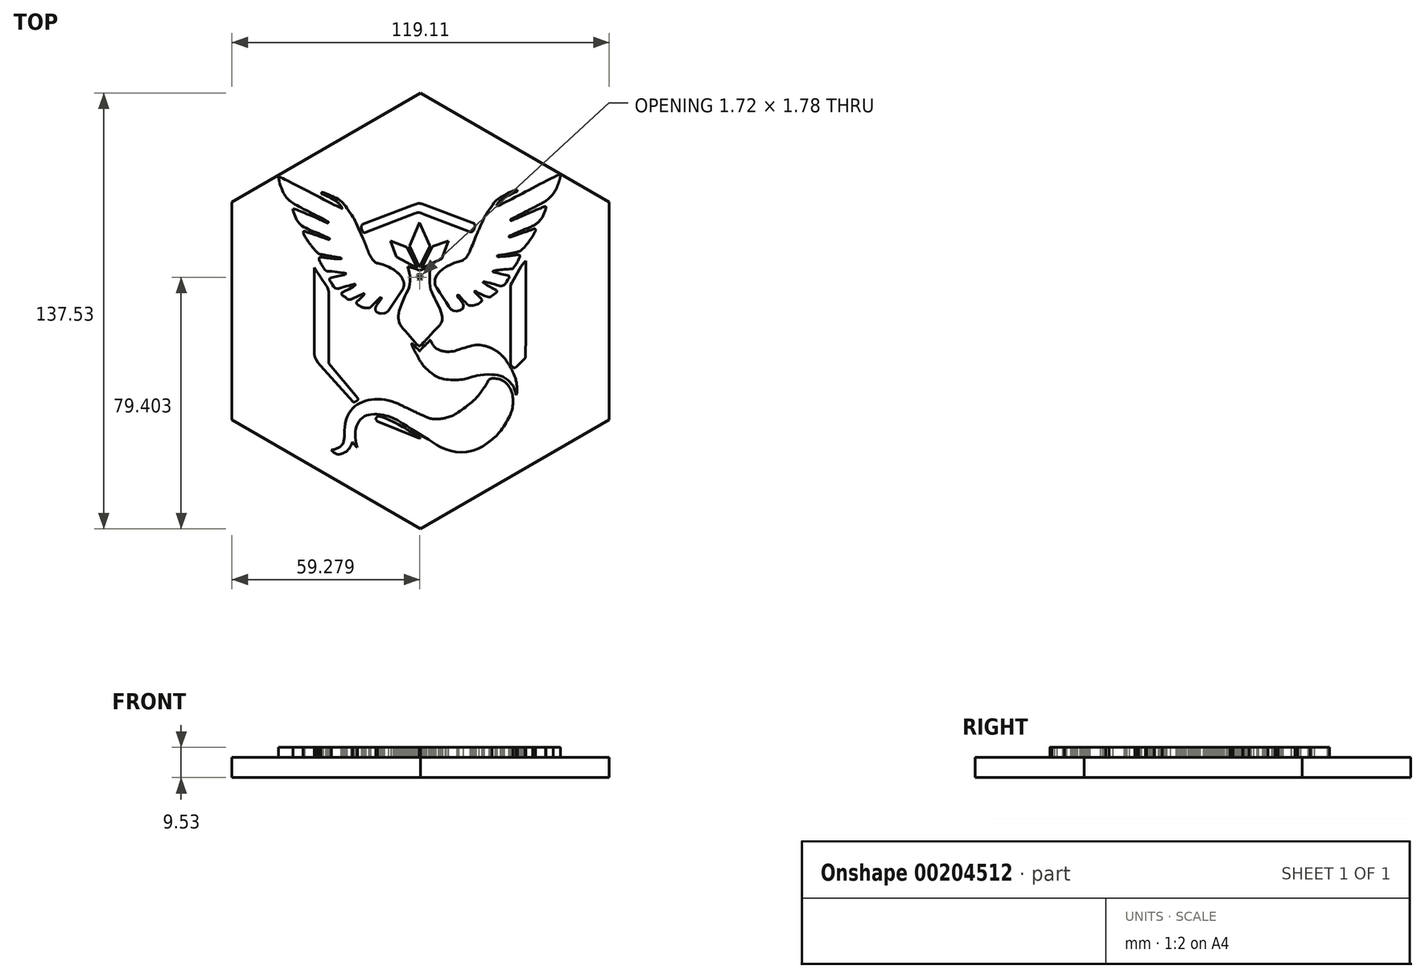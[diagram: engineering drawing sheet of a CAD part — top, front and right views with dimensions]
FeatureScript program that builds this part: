
annotation { "Feature Type Name" : "Feature", "Feature Type Description" : "" }
export const myFeature = defineFeature(function(context is Context, id is Id, definition is map)
    precondition{}
    {
        {
            var Q0;
            Q0=qCreatedBy(makeId("Top.planeOp"),FACE);
            var sketch = newSketch(context, id + "F0", { "sketchPlane" : qUnion([Q0])});
            skCircle(sketch, "E0.cCircle", {"center": v(-105.63, 45.8) * mm, "radius": 59.55 * mm, "construction": true});
            skLineSegment(sketch, "E0.0", {"start": v(-46.08, 80.2) * mm, "end": v(-46.08, 11.43) * mm});
            skLineSegment(sketch, "E0.1", {"start": v(-46.08, 11.43) * mm, "end": v(-105.63, -22.96) * mm});
            skLineSegment(sketch, "E0.2", {"start": v(-105.63, -22.96) * mm, "end": v(-165.19, 11.43) * mm});
            skLineSegment(sketch, "E0.3", {"start": v(-165.19, 11.43) * mm, "end": v(-165.19, 80.2) * mm});
            skLineSegment(sketch, "E0.4", {"start": v(-165.19, 80.2) * mm, "end": v(-105.63, 114.57) * mm});
            skLineSegment(sketch, "E0.5", {"start": v(-105.63, 114.57) * mm, "end": v(-46.08, 80.2) * mm});
            skPoint(sketch, "E0.0.midPoint", {"position": v(-46.08, 45.8) * mm});
            skSolve(sketch);
        }
        {
            var Q0;
            Q0 = qSketchRegion(id + "F0", true);
            extrude(context, id + "F1", {"entities" : qUnion([Q0]), "depth" : 6.35 * mm});
        }
        {
            var Q0;
            Q0=makeQuery(id+"F1.opExtrude","CAP_FACE",FACE,{"disambiguationData":[OSD([sQuery(id+"F0.wireOp",EDGE,"E0.0"),sQuery(id+"F0.wireOp",EDGE,"E0.1"),sQuery(id+"F0.wireOp",EDGE,"E0.2"),sQuery(id+"F0.wireOp",EDGE,"E0.3"),sQuery(id+"F0.wireOp",EDGE,"E0.4"),sQuery(id+"F0.wireOp",EDGE,"E0.5")])],"isStart":false});
            var sketch = newSketch(context, id + "F2", { "sketchPlane" : qUnion([Q0])});
            skLineSegment(sketch, "E1", {"start": v(-105.95, 58.52) * mm, "end": v(-106.29, 58.67) * mm});
            skLineSegment(sketch, "E2", {"start": v(-106.29, 58.67) * mm, "end": v(-106.82, 58.9) * mm});
            skLineSegment(sketch, "E3", {"start": v(-106.82, 58.9) * mm, "end": v(-107.22, 59.06) * mm});
            skLineSegment(sketch, "E4", {"start": v(-107.22, 59.06) * mm, "end": v(-107.95, 59.33) * mm});
            skLineSegment(sketch, "E5", {"start": v(-107.95, 59.33) * mm, "end": v(-108.51, 59.51) * mm});
            skLineSegment(sketch, "E6", {"start": v(-108.51, 59.51) * mm, "end": v(-109.32, 59.76) * mm});
            skLineSegment(sketch, "E7", {"start": v(-109.32, 59.76) * mm, "end": v(-109.7, 59.85) * mm});
            skLineSegment(sketch, "E8", {"start": v(-109.7, 59.85) * mm, "end": v(-109.79, 59.79) * mm});
            skLineSegment(sketch, "E9", {"start": v(-109.79, 59.79) * mm, "end": v(-109.65, 59.44) * mm});
            skLineSegment(sketch, "E10", {"start": v(-109.65, 59.44) * mm, "end": v(-109.46, 58.9) * mm});
            skLineSegment(sketch, "E11", {"start": v(-109.46, 58.9) * mm, "end": v(-109.37, 58.6) * mm});
            skLineSegment(sketch, "E12", {"start": v(-109.37, 58.6) * mm, "end": v(-109.17, 57.9) * mm});
            skLineSegment(sketch, "E13", {"start": v(-109.17, 57.9) * mm, "end": v(-109.04, 57.37) * mm});
            skLineSegment(sketch, "E14", {"start": v(-109.04, 57.37) * mm, "end": v(-109, 57.21) * mm});
            skLineSegment(sketch, "E15", {"start": v(-109, 57.21) * mm, "end": v(-108.96, 57.03) * mm});
            skLineSegment(sketch, "E16", {"start": v(-108.96, 57.03) * mm, "end": v(-108.93, 56.79) * mm});
            skLineSegment(sketch, "E17", {"start": v(-108.93, 56.79) * mm, "end": v(-108.9, 56.59) * mm});
            skLineSegment(sketch, "E18", {"start": v(-108.9, 56.59) * mm, "end": v(-108.9, 56.35) * mm});
            skLineSegment(sketch, "E19", {"start": v(-108.9, 56.35) * mm, "end": v(-108.9, 55.84) * mm});
            skLineSegment(sketch, "E20", {"start": v(-108.9, 55.84) * mm, "end": v(-108.9, 55.38) * mm});
            skLineSegment(sketch, "E21", {"start": v(-108.9, 55.38) * mm, "end": v(-108.95, 54.97) * mm});
            skLineSegment(sketch, "E22", {"start": v(-108.95, 54.97) * mm, "end": v(-109.05, 54.26) * mm});
            skLineSegment(sketch, "E23", {"start": v(-109.05, 54.26) * mm, "end": v(-109.25, 53.39) * mm});
            skLineSegment(sketch, "E24", {"start": v(-109.25, 53.39) * mm, "end": v(-109.54, 52.6) * mm});
            skLineSegment(sketch, "E25", {"start": v(-109.54, 52.6) * mm, "end": v(-109.84, 52.02) * mm});
            skLineSegment(sketch, "E26", {"start": v(-109.84, 52.02) * mm, "end": v(-110.15, 51.41) * mm});
            skLineSegment(sketch, "E27", {"start": v(-110.15, 51.41) * mm, "end": v(-110.62, 50.4) * mm});
            skLineSegment(sketch, "E28", {"start": v(-110.62, 50.4) * mm, "end": v(-111.05, 49.3) * mm});
            skLineSegment(sketch, "E29", {"start": v(-111.05, 49.3) * mm, "end": v(-111.43, 48.31) * mm});
            skLineSegment(sketch, "E30", {"start": v(-111.43, 48.31) * mm, "end": v(-111.58, 47.94) * mm});
            skLineSegment(sketch, "E31", {"start": v(-111.58, 47.94) * mm, "end": v(-112.06, 46.65) * mm});
            skLineSegment(sketch, "E32", {"start": v(-112.06, 46.65) * mm, "end": v(-112.35, 45.87) * mm});
            skLineSegment(sketch, "E33", {"start": v(-112.35, 45.87) * mm, "end": v(-112.58, 45.1) * mm});
            skLineSegment(sketch, "E34", {"start": v(-112.58, 45.1) * mm, "end": v(-112.68, 44.28) * mm});
            skLineSegment(sketch, "E35", {"start": v(-112.68, 44.28) * mm, "end": v(-112.68, 43.53) * mm});
            skLineSegment(sketch, "E36", {"start": v(-112.68, 43.53) * mm, "end": v(-112.57, 42.9) * mm});
            skLineSegment(sketch, "E37", {"start": v(-112.57, 42.9) * mm, "end": v(-112.35, 42.15) * mm});
            skLineSegment(sketch, "E38", {"start": v(-112.35, 42.15) * mm, "end": v(-112.1, 41.52) * mm});
            skLineSegment(sketch, "E39", {"start": v(-112.1, 41.52) * mm, "end": v(-111.7, 40.94) * mm});
            skLineSegment(sketch, "E40", {"start": v(-111.7, 40.94) * mm, "end": v(-111.49, 40.65) * mm});
            skLineSegment(sketch, "E41", {"start": v(-111.49, 40.65) * mm, "end": v(-111.2, 40.3) * mm});
            skLineSegment(sketch, "E42", {"start": v(-111.2, 40.3) * mm, "end": v(-110.46, 39.48) * mm});
            skLineSegment(sketch, "E43", {"start": v(-110.46, 39.48) * mm, "end": v(-109.6, 38.53) * mm});
            skLineSegment(sketch, "E44", {"start": v(-109.6, 38.53) * mm, "end": v(-108.33, 37.04) * mm});
            skLineSegment(sketch, "E45", {"start": v(-108.33, 37.04) * mm, "end": v(-106.77, 35.22) * mm});
            skLineSegment(sketch, "E46", {"start": v(-106.77, 35.22) * mm, "end": v(-106.6, 35.03) * mm});
            skLineSegment(sketch, "E47", {"start": v(-106.6, 35.03) * mm, "end": v(-106.49, 34.93) * mm});
            skLineSegment(sketch, "E48", {"start": v(-106.49, 34.93) * mm, "end": v(-106.32, 34.81) * mm});
            skLineSegment(sketch, "E49", {"start": v(-106.32, 34.81) * mm, "end": v(-106.22, 34.77) * mm});
            skLineSegment(sketch, "E50", {"start": v(-106.22, 34.77) * mm, "end": v(-106.16, 34.76) * mm});
            skLineSegment(sketch, "E51", {"start": v(-106.16, 34.76) * mm, "end": v(-106.07, 34.74) * mm});
            skLineSegment(sketch, "E52", {"start": v(-106.07, 34.74) * mm, "end": v(-106, 34.74) * mm});
            skLineSegment(sketch, "E53", {"start": v(-106, 34.74) * mm, "end": v(-105.94, 34.76) * mm});
            skLineSegment(sketch, "E54", {"start": v(-105.94, 34.76) * mm, "end": v(-105.8, 34.8) * mm});
            skLineSegment(sketch, "E55", {"start": v(-105.8, 34.8) * mm, "end": v(-105.6, 34.9) * mm});
            skLineSegment(sketch, "E56", {"start": v(-105.6, 34.9) * mm, "end": v(-105.35, 35.1) * mm});
            skLineSegment(sketch, "E57", {"start": v(-105.35, 35.1) * mm, "end": v(-105.2, 35.26) * mm});
            skLineSegment(sketch, "E58", {"start": v(-105.2, 35.26) * mm, "end": v(-104.74, 35.8) * mm});
            skLineSegment(sketch, "E59", {"start": v(-104.74, 35.8) * mm, "end": v(-104.6, 35.96) * mm});
            skLineSegment(sketch, "E60", {"start": v(-104.6, 35.96) * mm, "end": v(-104.43, 36.14) * mm});
            skLineSegment(sketch, "E61", {"start": v(-104.43, 36.14) * mm, "end": v(-104.3, 36.28) * mm});
            skLineSegment(sketch, "E62", {"start": v(-104.3, 36.28) * mm, "end": v(-104.14, 36.47) * mm});
            skLineSegment(sketch, "E63", {"start": v(-104.14, 36.47) * mm, "end": v(-103.74, 36.92) * mm});
            skLineSegment(sketch, "E64", {"start": v(-103.74, 36.92) * mm, "end": v(-103.2, 37.48) * mm});
            skLineSegment(sketch, "E65", {"start": v(-103.2, 37.48) * mm, "end": v(-102.48, 38.25) * mm});
            skLineSegment(sketch, "E66", {"start": v(-102.48, 38.25) * mm, "end": v(-101.42, 39.4) * mm});
            skLineSegment(sketch, "E67", {"start": v(-101.42, 39.4) * mm, "end": v(-100.82, 40.06) * mm});
            skLineSegment(sketch, "E68", {"start": v(-100.82, 40.06) * mm, "end": v(-100.12, 40.81) * mm});
            skLineSegment(sketch, "E69", {"start": v(-100.12, 40.81) * mm, "end": v(-99.61, 41.34) * mm});
            skLineSegment(sketch, "E70", {"start": v(-99.61, 41.34) * mm, "end": v(-99.38, 41.59) * mm});
            skLineSegment(sketch, "E71", {"start": v(-99.38, 41.59) * mm, "end": v(-99.14, 41.97) * mm});
            skLineSegment(sketch, "E72", {"start": v(-99.14, 41.97) * mm, "end": v(-98.94, 42.4) * mm});
            skLineSegment(sketch, "E73", {"start": v(-98.94, 42.4) * mm, "end": v(-98.87, 42.82) * mm});
            skLineSegment(sketch, "E74", {"start": v(-98.87, 42.82) * mm, "end": v(-98.85, 43.2) * mm});
            skLineSegment(sketch, "E75", {"start": v(-98.85, 43.2) * mm, "end": v(-98.86, 43.77) * mm});
            skPoint(sketch, "E75.endSnap0", {"position": v(-98.86, 43) * mm});
            skLineSegment(sketch, "E76", {"start": v(-98.86, 43.77) * mm, "end": v(-98.87, 44.15) * mm});
            skLineSegment(sketch, "E77", {"start": v(-98.87, 44.15) * mm, "end": v(-98.92, 44.54) * mm});
            skLineSegment(sketch, "E78", {"start": v(-98.92, 44.54) * mm, "end": v(-99.02, 44.95) * mm});
            skLineSegment(sketch, "E79", {"start": v(-99.02, 44.95) * mm, "end": v(-99.06, 45.1) * mm});
            skLineSegment(sketch, "E80", {"start": v(-99.06, 45.1) * mm, "end": v(-99.14, 45.35) * mm});
            skLineSegment(sketch, "E81", {"start": v(-99.14, 45.35) * mm, "end": v(-99.28, 45.73) * mm});
            skLineSegment(sketch, "E82", {"start": v(-99.28, 45.73) * mm, "end": v(-99.5, 46.31) * mm});
            skLineSegment(sketch, "E83", {"start": v(-99.5, 46.31) * mm, "end": v(-99.64, 46.64) * mm});
            skLineSegment(sketch, "E84", {"start": v(-99.64, 46.64) * mm, "end": v(-99.82, 47.07) * mm});
            skLineSegment(sketch, "E85", {"start": v(-99.82, 47.07) * mm, "end": v(-99.95, 47.37) * mm});
            skLineSegment(sketch, "E86", {"start": v(-99.95, 47.37) * mm, "end": v(-100.21, 47.87) * mm});
            skLineSegment(sketch, "E87", {"start": v(-100.21, 47.87) * mm, "end": v(-100.38, 48.2) * mm});
            skLineSegment(sketch, "E88", {"start": v(-100.38, 48.2) * mm, "end": v(-100.63, 48.68) * mm});
            skLineSegment(sketch, "E89", {"start": v(-100.63, 48.68) * mm, "end": v(-100.8, 49) * mm});
            skLineSegment(sketch, "E90", {"start": v(-100.8, 49) * mm, "end": v(-100.92, 49.29) * mm});
            skLineSegment(sketch, "E91", {"start": v(-100.92, 49.29) * mm, "end": v(-101, 49.5) * mm});
            skLineSegment(sketch, "E92", {"start": v(-101, 49.5) * mm, "end": v(-101.17, 49.87) * mm});
            skLineSegment(sketch, "E93", {"start": v(-101.17, 49.87) * mm, "end": v(-101.35, 50.22) * mm});
            skLineSegment(sketch, "E94", {"start": v(-101.35, 50.22) * mm, "end": v(-101.5, 50.52) * mm});
            skLineSegment(sketch, "E95", {"start": v(-101.5, 50.52) * mm, "end": v(-101.72, 50.93) * mm});
            skLineSegment(sketch, "E96", {"start": v(-101.72, 50.93) * mm, "end": v(-101.95, 51.41) * mm});
            skLineSegment(sketch, "E97", {"start": v(-101.95, 51.41) * mm, "end": v(-102.15, 51.83) * mm});
            skLineSegment(sketch, "E98", {"start": v(-102.15, 51.83) * mm, "end": v(-102.27, 52.07) * mm});
            skLineSegment(sketch, "E99", {"start": v(-105.95, 58.52) * mm, "end": v(-105.59, 58.69) * mm});
            skLineSegment(sketch, "E100", {"start": v(-105.59, 58.69) * mm, "end": v(-104.96, 58.94) * mm});
            skLineSegment(sketch, "E101", {"start": v(-104.96, 58.94) * mm, "end": v(-104.44, 59.14) * mm});
            skLineSegment(sketch, "E102", {"start": v(-104.44, 59.14) * mm, "end": v(-103.95, 59.3) * mm});
            skLineSegment(sketch, "E103", {"start": v(-103.95, 59.3) * mm, "end": v(-103.54, 59.46) * mm});
            skLineSegment(sketch, "E104", {"start": v(-103.54, 59.46) * mm, "end": v(-103.02, 59.67) * mm});
            skLineSegment(sketch, "E105", {"start": v(-103.02, 59.67) * mm, "end": v(-102.64, 59.82) * mm});
            skLineSegment(sketch, "E106", {"start": v(-102.64, 59.82) * mm, "end": v(-102.58, 59.82) * mm});
            skLineSegment(sketch, "E107", {"start": v(-102.58, 59.82) * mm, "end": v(-102.55, 59.8) * mm});
            skLineSegment(sketch, "E108", {"start": v(-102.55, 59.8) * mm, "end": v(-102.55, 59.52) * mm});
            skLineSegment(sketch, "E109", {"start": v(-102.27, 52.07) * mm, "end": v(-102.4, 52.35) * mm});
            skLineSegment(sketch, "E110", {"start": v(-102.4, 52.35) * mm, "end": v(-102.48, 52.64) * mm});
            skLineSegment(sketch, "E111", {"start": v(-102.48, 52.64) * mm, "end": v(-102.54, 53.04) * mm});
            skLineSegment(sketch, "E112", {"start": v(-102.54, 53.04) * mm, "end": v(-102.63, 53.68) * mm});
            skLineSegment(sketch, "E113", {"start": v(-102.63, 53.68) * mm, "end": v(-102.71, 54.65) * mm});
            skLineSegment(sketch, "E114", {"start": v(-102.71, 54.65) * mm, "end": v(-102.71, 55.48) * mm});
            skLineSegment(sketch, "E115", {"start": v(-102.71, 55.48) * mm, "end": v(-102.71, 56.32) * mm});
            skLineSegment(sketch, "E116", {"start": v(-102.71, 56.32) * mm, "end": v(-102.71, 56.75) * mm});
            skLineSegment(sketch, "E117", {"start": v(-102.71, 56.75) * mm, "end": v(-102.71, 57.5) * mm});
            skLineSegment(sketch, "E118", {"start": v(-102.55, 59.52) * mm, "end": v(-102.58, 59.26) * mm});
            skLineSegment(sketch, "E119", {"start": v(-102.58, 59.26) * mm, "end": v(-102.62, 58.84) * mm});
            skLineSegment(sketch, "E120", {"start": v(-102.62, 58.84) * mm, "end": v(-102.65, 58.54) * mm});
            skLineSegment(sketch, "E121", {"start": v(-102.65, 58.54) * mm, "end": v(-102.68, 58.08) * mm});
            skLineSegment(sketch, "E122", {"start": v(-102.68, 58.08) * mm, "end": v(-102.71, 57.5) * mm});
            skLineSegment(sketch, "E123", {"start": v(-106.77, 57.1) * mm, "end": v(-105.9, 55.57) * mm});
            skLineSegment(sketch, "E124", {"start": v(-105.9, 55.57) * mm, "end": v(-105.86, 55.55) * mm});
            skLineSegment(sketch, "E125", {"start": v(-105.86, 55.55) * mm, "end": v(-105.83, 55.57) * mm});
            skLineSegment(sketch, "E126", {"start": v(-105.83, 55.57) * mm, "end": v(-105.05, 57.1) * mm});
            skLineSegment(sketch, "E127", {"start": v(-106.77, 57.1) * mm, "end": v(-106.65, 57.17) * mm});
            skLineSegment(sketch, "E128", {"start": v(-106.65, 57.17) * mm, "end": v(-106.44, 57.25) * mm});
            skLineSegment(sketch, "E129", {"start": v(-106.44, 57.25) * mm, "end": v(-106.2, 57.32) * mm});
            skLineSegment(sketch, "E130", {"start": v(-105.05, 57.1) * mm, "end": v(-105.2, 57.22) * mm});
            skLineSegment(sketch, "E131", {"start": v(-105.2, 57.22) * mm, "end": v(-105.44, 57.3) * mm});
            skLineSegment(sketch, "E132", {"start": v(-105.44, 57.3) * mm, "end": v(-105.65, 57.33) * mm});
            skLineSegment(sketch, "E133", {"start": v(-105.65, 57.33) * mm, "end": v(-106.05, 57.33) * mm});
            skLineSegment(sketch, "E134", {"start": v(-106.05, 57.33) * mm, "end": v(-106.2, 57.32) * mm});
            skLineSegment(sketch, "E135", {"start": v(-139.25, 59.36) * mm, "end": v(-139.25, 32.34) * mm});
            skLineSegment(sketch, "E136", {"start": v(-139.25, 32.34) * mm, "end": v(-139.04, 31.44) * mm});
            skLineSegment(sketch, "E137", {"start": v(-139.04, 31.44) * mm, "end": v(-138.6, 30.43) * mm});
            skLineSegment(sketch, "E138", {"start": v(-138.6, 30.43) * mm, "end": v(-138, 29.46) * mm});
            skLineSegment(sketch, "E139", {"start": v(-138, 29.46) * mm, "end": v(-137.23, 28.51) * mm});
            skLineSegment(sketch, "E140", {"start": v(-137.23, 28.51) * mm, "end": v(-127.07, 17.2) * mm});
            skLineSegment(sketch, "E141", {"start": v(-127.07, 17.2) * mm, "end": v(-126.8, 17.07) * mm});
            skLineSegment(sketch, "E142", {"start": v(-126.8, 17.07) * mm, "end": v(-126.52, 17.07) * mm});
            skLineSegment(sketch, "E143", {"start": v(-126.52, 17.07) * mm, "end": v(-126.4, 17.1) * mm});
            skLineSegment(sketch, "E144", {"start": v(-126.4, 17.1) * mm, "end": v(-125.48, 17.68) * mm});
            skLineSegment(sketch, "E145", {"start": v(-125.48, 17.68) * mm, "end": v(-125.43, 17.78) * mm});
            skLineSegment(sketch, "E146", {"start": v(-125.43, 17.78) * mm, "end": v(-125.39, 17.93) * mm});
            skLineSegment(sketch, "E147", {"start": v(-125.39, 17.93) * mm, "end": v(-125.39, 18.08) * mm});
            skLineSegment(sketch, "E148", {"start": v(-125.39, 18.08) * mm, "end": v(-125.43, 18.23) * mm});
            skLineSegment(sketch, "E149", {"start": v(-125.43, 18.23) * mm, "end": v(-125.51, 18.36) * mm});
            skLineSegment(sketch, "E150", {"start": v(-125.51, 18.36) * mm, "end": v(-128.32, 21.74) * mm});
            skLineSegment(sketch, "E151", {"start": v(-128.32, 21.74) * mm, "end": v(-131.78, 25.92) * mm});
            skLineSegment(sketch, "E152", {"start": v(-131.78, 25.92) * mm, "end": v(-134.23, 28.87) * mm});
            skLineSegment(sketch, "E153", {"start": v(-134.23, 28.87) * mm, "end": v(-134.38, 29.06) * mm});
            skLineSegment(sketch, "E154", {"start": v(-134.38, 29.06) * mm, "end": v(-134.58, 29.3) * mm});
            skLineSegment(sketch, "E155", {"start": v(-134.58, 29.3) * mm, "end": v(-134.6, 29.4) * mm});
            skLineSegment(sketch, "E156", {"start": v(-134.6, 29.4) * mm, "end": v(-134.6, 29.52) * mm});
            skLineSegment(sketch, "E157", {"start": v(-134.6, 29.52) * mm, "end": v(-134.6, 50.94) * mm});
            skLineSegment(sketch, "E158", {"start": v(-134.6, 50.94) * mm, "end": v(-134.6, 51.2) * mm});
            skLineSegment(sketch, "E159", {"start": v(-134.6, 51.2) * mm, "end": v(-134.6, 51.52) * mm});
            skLineSegment(sketch, "E160", {"start": v(-134.6, 51.52) * mm, "end": v(-134.64, 51.8) * mm});
            skLineSegment(sketch, "E161", {"start": v(-134.64, 51.8) * mm, "end": v(-134.76, 52.4) * mm});
            skLineSegment(sketch, "E162", {"start": v(-134.76, 52.4) * mm, "end": v(-134.87, 52.76) * mm});
            skLineSegment(sketch, "E163", {"start": v(-134.87, 52.76) * mm, "end": v(-135.05, 53.17) * mm});
            skLineSegment(sketch, "E164", {"start": v(-135.05, 53.17) * mm, "end": v(-135.32, 53.68) * mm});
            skLineSegment(sketch, "E165", {"start": v(-135.32, 53.68) * mm, "end": v(-135.63, 54.17) * mm});
            skLineSegment(sketch, "E166", {"start": v(-135.63, 54.17) * mm, "end": v(-136.15, 54.9) * mm});
            skLineSegment(sketch, "E167", {"start": v(-136.15, 54.9) * mm, "end": v(-136.53, 55.44) * mm});
            skLineSegment(sketch, "E168", {"start": v(-136.53, 55.44) * mm, "end": v(-137.02, 56.19) * mm});
            skLineSegment(sketch, "E169", {"start": v(-137.02, 56.19) * mm, "end": v(-137.16, 56.38) * mm});
            skLineSegment(sketch, "E170", {"start": v(-139.25, 59.36) * mm, "end": v(-139.22, 59.38) * mm});
            skLineSegment(sketch, "E171", {"start": v(-139.22, 59.38) * mm, "end": v(-139.2, 59.4) * mm});
            skLineSegment(sketch, "E172", {"start": v(-139.2, 59.4) * mm, "end": v(-139.16, 59.4) * mm});
            skLineSegment(sketch, "E173", {"start": v(-139.16, 59.4) * mm, "end": v(-139.13, 59.38) * mm});
            skLineSegment(sketch, "E174", {"start": v(-139.13, 59.38) * mm, "end": v(-139.06, 59.28) * mm});
            skLineSegment(sketch, "E175", {"start": v(-139.06, 59.28) * mm, "end": v(-138.96, 59.12) * mm});
            skLineSegment(sketch, "E176", {"start": v(-138.96, 59.12) * mm, "end": v(-138.78, 58.82) * mm});
            skLineSegment(sketch, "E177", {"start": v(-138.78, 58.82) * mm, "end": v(-138.62, 58.59) * mm});
            skLineSegment(sketch, "E178", {"start": v(-138.62, 58.59) * mm, "end": v(-138.53, 58.44) * mm});
            skLineSegment(sketch, "E179", {"start": v(-138.53, 58.44) * mm, "end": v(-138.35, 58.16) * mm});
            skLineSegment(sketch, "E180", {"start": v(-138.35, 58.16) * mm, "end": v(-138.16, 57.88) * mm});
            skLineSegment(sketch, "E181", {"start": v(-138.16, 57.88) * mm, "end": v(-137.92, 57.51) * mm});
            skLineSegment(sketch, "E182", {"start": v(-137.92, 57.51) * mm, "end": v(-137.7, 57.2) * mm});
            skLineSegment(sketch, "E183", {"start": v(-137.7, 57.2) * mm, "end": v(-137.16, 56.38) * mm});
            skLineSegment(sketch, "E184", {"start": v(-123.9, 73.14) * mm, "end": v(-124.15, 72.97) * mm});
            skLineSegment(sketch, "E185", {"start": v(-124.15, 72.97) * mm, "end": v(-124.3, 72.8) * mm});
            skLineSegment(sketch, "E186", {"start": v(-124.3, 72.8) * mm, "end": v(-124.4, 72.63) * mm});
            skLineSegment(sketch, "E187", {"start": v(-124.4, 72.63) * mm, "end": v(-124.4, 72.34) * mm});
            skLineSegment(sketch, "E188", {"start": v(-124.4, 72.34) * mm, "end": v(-124.4, 72.03) * mm});
            skLineSegment(sketch, "E189", {"start": v(-124.4, 72.03) * mm, "end": v(-124.36, 71.82) * mm});
            skLineSegment(sketch, "E190", {"start": v(-124.36, 71.82) * mm, "end": v(-124.24, 71.47) * mm});
            skLineSegment(sketch, "E191", {"start": v(-124.24, 71.47) * mm, "end": v(-124, 70.95) * mm});
            skLineSegment(sketch, "E192", {"start": v(-124, 70.95) * mm, "end": v(-123.64, 70.62) * mm});
            skLineSegment(sketch, "E193", {"start": v(-123.64, 70.62) * mm, "end": v(-123.46, 70.56) * mm});
            skLineSegment(sketch, "E194", {"start": v(-123.46, 70.56) * mm, "end": v(-123.33, 70.56) * mm});
            skLineSegment(sketch, "E195", {"start": v(-123.33, 70.56) * mm, "end": v(-122.93, 70.65) * mm});
            skLineSegment(sketch, "E196", {"start": v(-122.93, 70.65) * mm, "end": v(-107.4, 76.64) * mm});
            skLineSegment(sketch, "E197", {"start": v(-107.4, 76.64) * mm, "end": v(-106.97, 76.76) * mm});
            skLineSegment(sketch, "E198", {"start": v(-106.97, 76.76) * mm, "end": v(-106.63, 76.82) * mm});
            skLineSegment(sketch, "E199", {"start": v(-106.63, 76.82) * mm, "end": v(-106.1, 76.82) * mm});
            skLineSegment(sketch, "E200", {"start": v(-106.1, 76.82) * mm, "end": v(-105.56, 76.7) * mm});
            skLineSegment(sketch, "E201", {"start": v(-105.56, 76.7) * mm, "end": v(-105.17, 76.56) * mm});
            skLineSegment(sketch, "E202", {"start": v(-105.17, 76.56) * mm, "end": v(-104.44, 76.29) * mm});
            skLineSegment(sketch, "E203", {"start": v(-104.44, 76.29) * mm, "end": v(-90.65, 70.96) * mm});
            skLineSegment(sketch, "E204", {"start": v(-90.65, 70.96) * mm, "end": v(-90.1, 70.75) * mm});
            skLineSegment(sketch, "E205", {"start": v(-90.1, 70.75) * mm, "end": v(-89.81, 70.72) * mm});
            skLineSegment(sketch, "E206", {"start": v(-89.81, 70.72) * mm, "end": v(-89.54, 70.76) * mm});
            skLineSegment(sketch, "E207", {"start": v(-89.54, 70.76) * mm, "end": v(-89.29, 70.86) * mm});
            skLineSegment(sketch, "E208", {"start": v(-89.29, 70.86) * mm, "end": v(-89.1, 71.08) * mm});
            skLineSegment(sketch, "E209", {"start": v(-89.1, 71.08) * mm, "end": v(-88.94, 71.24) * mm});
            skLineSegment(sketch, "E210", {"start": v(-88.94, 71.24) * mm, "end": v(-88.5, 72.4) * mm});
            skLineSegment(sketch, "E211", {"start": v(-88.5, 72.4) * mm, "end": v(-88.43, 72.73) * mm});
            skLineSegment(sketch, "E212", {"start": v(-88.43, 72.73) * mm, "end": v(-88.46, 72.99) * mm});
            skLineSegment(sketch, "E213", {"start": v(-88.46, 72.99) * mm, "end": v(-88.55, 73.2) * mm});
            skLineSegment(sketch, "E214", {"start": v(-88.55, 73.2) * mm, "end": v(-88.8, 73.38) * mm});
            skLineSegment(sketch, "E215", {"start": v(-88.8, 73.38) * mm, "end": v(-89.1, 73.51) * mm});
            skLineSegment(sketch, "E216", {"start": v(-89.1, 73.51) * mm, "end": v(-89.42, 73.65) * mm});
            skLineSegment(sketch, "E217", {"start": v(-89.42, 73.65) * mm, "end": v(-104.7, 79.41) * mm});
            skLineSegment(sketch, "E218", {"start": v(-104.7, 79.41) * mm, "end": v(-105.28, 79.63) * mm});
            skLineSegment(sketch, "E219", {"start": v(-105.28, 79.63) * mm, "end": v(-105.69, 79.72) * mm});
            skLineSegment(sketch, "E220", {"start": v(-105.69, 79.72) * mm, "end": v(-105.97, 79.75) * mm});
            skLineSegment(sketch, "E221", {"start": v(-105.97, 79.75) * mm, "end": v(-106.31, 79.75) * mm});
            skLineSegment(sketch, "E222", {"start": v(-106.31, 79.75) * mm, "end": v(-106.62, 79.71) * mm});
            skLineSegment(sketch, "E223", {"start": v(-106.62, 79.71) * mm, "end": v(-106.9, 79.6) * mm});
            skLineSegment(sketch, "E224", {"start": v(-106.9, 79.6) * mm, "end": v(-107.45, 79.4) * mm});
            skLineSegment(sketch, "E225", {"start": v(-107.45, 79.4) * mm, "end": v(-108.16, 79.11) * mm});
            skLineSegment(sketch, "E226", {"start": v(-108.16, 79.11) * mm, "end": v(-123.9, 73.14) * mm});
            skLineSegment(sketch, "E227", {"start": v(-106.08, 5.59) * mm, "end": v(-119.25, 10.97) * mm});
            skLineSegment(sketch, "E228", {"start": v(-119.25, 10.97) * mm, "end": v(-119.43, 11.13) * mm});
            skLineSegment(sketch, "E229", {"start": v(-119.43, 11.13) * mm, "end": v(-119.74, 11.63) * mm});
            skLineSegment(sketch, "E230", {"start": v(-119.74, 11.63) * mm, "end": v(-119.78, 11.8) * mm});
            skLineSegment(sketch, "E231", {"start": v(-119.78, 11.8) * mm, "end": v(-119.78, 12.02) * mm});
            skLineSegment(sketch, "E232", {"start": v(-119.78, 12.02) * mm, "end": v(-119.63, 12.1) * mm});
            skLineSegment(sketch, "E233", {"start": v(-119.63, 12.1) * mm, "end": v(-119.38, 12.32) * mm});
            skLineSegment(sketch, "E234", {"start": v(-119.38, 12.32) * mm, "end": v(-119.13, 12.6) * mm});
            skLineSegment(sketch, "E235", {"start": v(-119.13, 12.6) * mm, "end": v(-119.07, 12.64) * mm});
            skLineSegment(sketch, "E236", {"start": v(-119.07, 12.64) * mm, "end": v(-119, 12.64) * mm});
            skLineSegment(sketch, "E237", {"start": v(-119, 12.64) * mm, "end": v(-118.86, 12.6) * mm});
            skLineSegment(sketch, "E238", {"start": v(-118.86, 12.6) * mm, "end": v(-118.74, 12.56) * mm});
            skLineSegment(sketch, "E239", {"start": v(-118.74, 12.56) * mm, "end": v(-118.56, 12.5) * mm});
            skLineSegment(sketch, "E240", {"start": v(-118.56, 12.5) * mm, "end": v(-118.32, 12.44) * mm});
            skLineSegment(sketch, "E241", {"start": v(-118.32, 12.44) * mm, "end": v(-117.9, 12.34) * mm});
            skLineSegment(sketch, "E242", {"start": v(-117.9, 12.34) * mm, "end": v(-117.42, 12.24) * mm});
            skLineSegment(sketch, "E243", {"start": v(-117.42, 12.24) * mm, "end": v(-117.3, 12.19) * mm});
            skLineSegment(sketch, "E244", {"start": v(-117.3, 12.19) * mm, "end": v(-114.26, 10.85) * mm});
            skLineSegment(sketch, "E245", {"start": v(-114.26, 10.85) * mm, "end": v(-113.8, 10.63) * mm});
            skLineSegment(sketch, "E246", {"start": v(-113.8, 10.63) * mm, "end": v(-113.53, 10.51) * mm});
            skLineSegment(sketch, "E247", {"start": v(-113.53, 10.51) * mm, "end": v(-113.42, 10.46) * mm});
            skLineSegment(sketch, "E248", {"start": v(-113.42, 10.46) * mm, "end": v(-113.24, 10.34) * mm});
            skLineSegment(sketch, "E249", {"start": v(-113.24, 10.34) * mm, "end": v(-112.52, 9.94) * mm});
            skLineSegment(sketch, "E250", {"start": v(-112.52, 9.94) * mm, "end": v(-111.86, 9.57) * mm});
            skLineSegment(sketch, "E251", {"start": v(-111.86, 9.57) * mm, "end": v(-111.29, 9.23) * mm});
            skLineSegment(sketch, "E252", {"start": v(-111.29, 9.23) * mm, "end": v(-110.93, 9.02) * mm});
            skLineSegment(sketch, "E253", {"start": v(-110.93, 9.02) * mm, "end": v(-110.39, 8.7) * mm});
            skLineSegment(sketch, "E254", {"start": v(-110.39, 8.7) * mm, "end": v(-109.94, 8.4) * mm});
            skLineSegment(sketch, "E255", {"start": v(-106.08, 5.59) * mm, "end": v(-106, 5.59) * mm});
            skLineSegment(sketch, "E256", {"start": v(-106, 5.59) * mm, "end": v(-105.65, 5.76) * mm});
            skLineSegment(sketch, "E257", {"start": v(-105.65, 5.76) * mm, "end": v(-105.62, 5.82) * mm});
            skLineSegment(sketch, "E258", {"start": v(-105.62, 5.82) * mm, "end": v(-105.65, 5.86) * mm});
            skLineSegment(sketch, "E259", {"start": v(-105.65, 5.86) * mm, "end": v(-108.42, 7.45) * mm});
            skLineSegment(sketch, "E260", {"start": v(-109.94, 8.4) * mm, "end": v(-109.5, 8.1) * mm});
            skLineSegment(sketch, "E261", {"start": v(-109.5, 8.1) * mm, "end": v(-109.06, 7.8) * mm});
            skLineSegment(sketch, "E262", {"start": v(-109.06, 7.8) * mm, "end": v(-108.76, 7.64) * mm});
            skLineSegment(sketch, "E263", {"start": v(-108.76, 7.64) * mm, "end": v(-108.42, 7.45) * mm});
            skLineSegment(sketch, "E264", {"start": v(-77.24, 29.08) * mm, "end": v(-77.24, 53.6) * mm});
            skLineSegment(sketch, "E265", {"start": v(-77.24, 53.6) * mm, "end": v(-77.15, 54.04) * mm});
            skLineSegment(sketch, "E266", {"start": v(-77.15, 54.04) * mm, "end": v(-76.9, 54.61) * mm});
            skLineSegment(sketch, "E267", {"start": v(-76.9, 54.61) * mm, "end": v(-75.1, 57.76) * mm});
            skLineSegment(sketch, "E268", {"start": v(-75.1, 57.76) * mm, "end": v(-74.4, 58.98) * mm});
            skLineSegment(sketch, "E269", {"start": v(-74.4, 58.98) * mm, "end": v(-73.9, 59.8) * mm});
            skLineSegment(sketch, "E270", {"start": v(-73.9, 59.8) * mm, "end": v(-73.66, 60.17) * mm});
            skLineSegment(sketch, "E271", {"start": v(-73.66, 60.17) * mm, "end": v(-73.44, 60.48) * mm});
            skLineSegment(sketch, "E272", {"start": v(-73.44, 60.48) * mm, "end": v(-73.1, 60.9) * mm});
            skLineSegment(sketch, "E273", {"start": v(-73.1, 60.9) * mm, "end": v(-72.8, 61.25) * mm});
            skLineSegment(sketch, "E274", {"start": v(-72.8, 61.25) * mm, "end": v(-72.5, 61.53) * mm});
            skLineSegment(sketch, "E275", {"start": v(-72.5, 61.53) * mm, "end": v(-72.46, 61.56) * mm});
            skLineSegment(sketch, "E276", {"start": v(-72.46, 61.56) * mm, "end": v(-72.42, 61.56) * mm});
            skLineSegment(sketch, "E277", {"start": v(-72.42, 61.56) * mm, "end": v(-72.4, 61.53) * mm});
            skLineSegment(sketch, "E278", {"start": v(-72.4, 61.53) * mm, "end": v(-72.39, 61.46) * mm});
            skLineSegment(sketch, "E279", {"start": v(-72.39, 61.46) * mm, "end": v(-72.39, 58.37) * mm});
            skLineSegment(sketch, "E280", {"start": v(-72.39, 58.37) * mm, "end": v(-72.45, 57.5) * mm});
            skLineSegment(sketch, "E281", {"start": v(-72.45, 57.5) * mm, "end": v(-72.45, 39.82) * mm});
            skLineSegment(sketch, "E282", {"start": v(-72.45, 39.82) * mm, "end": v(-72.45, 37.74) * mm});
            skLineSegment(sketch, "E283", {"start": v(-72.45, 37.74) * mm, "end": v(-72.45, 35.98) * mm});
            skLineSegment(sketch, "E284", {"start": v(-72.45, 35.98) * mm, "end": v(-72.59, 33.5) * mm});
            skLineSegment(sketch, "E285", {"start": v(-72.59, 33.5) * mm, "end": v(-72.59, 31.04) * mm});
            skLineSegment(sketch, "E286", {"start": v(-72.59, 31.04) * mm, "end": v(-72.65, 30.87) * mm});
            skLineSegment(sketch, "E287", {"start": v(-72.65, 30.87) * mm, "end": v(-75.05, 28.53) * mm});
            skLineSegment(sketch, "E288", {"start": v(-75.05, 28.53) * mm, "end": v(-75.37, 28.18) * mm});
            skLineSegment(sketch, "E289", {"start": v(-75.37, 28.18) * mm, "end": v(-75.69, 27.91) * mm});
            skLineSegment(sketch, "E290", {"start": v(-75.69, 27.91) * mm, "end": v(-75.88, 27.86) * mm});
            skLineSegment(sketch, "E291", {"start": v(-75.88, 27.86) * mm, "end": v(-76.13, 27.86) * mm});
            skLineSegment(sketch, "E292", {"start": v(-76.13, 27.86) * mm, "end": v(-76.35, 27.94) * mm});
            skLineSegment(sketch, "E293", {"start": v(-76.35, 27.94) * mm, "end": v(-76.67, 28.22) * mm});
            skLineSegment(sketch, "E294", {"start": v(-76.67, 28.22) * mm, "end": v(-77.2, 28.8) * mm});
            skLineSegment(sketch, "E295", {"start": v(-77.24, 29.08) * mm, "end": v(-77.24, 28.9) * mm});
            skArc(sketch, "E296", {"start": v(-110.86, 54.43) * mm, "mid": v(-111.56, 56.33) * mm, "end": v(-112.9, 57.85) * mm});
            skArc(sketch, "E297", {"start": v(-111.35, 52.52) * mm, "mid": v(-110.98, 53.44) * mm, "end": v(-110.86, 54.43) * mm});
            skLineSegment(sketch, "E298", {"start": v(-111.35, 52.52) * mm, "end": v(-115.72, 45.97) * mm});
            skArc(sketch, "E299", {"start": v(-117.12, 45.1) * mm, "mid": v(-116.32, 45.38) * mm, "end": v(-115.72, 45.97) * mm});
            skLineSegment(sketch, "E300", {"start": v(-117.12, 45.1) * mm, "end": v(-118.26, 45.03) * mm});
            skArc(sketch, "E301", {"start": v(-119.68, 45.67) * mm, "mid": v(-119.03, 45.22) * mm, "end": v(-118.26, 45.03) * mm});
            skArc(sketch, "E302", {"start": v(-119.86, 46.9) * mm, "mid": v(-119.93, 46.26) * mm, "end": v(-119.68, 45.67) * mm});
            skArc(sketch, "E303", {"start": v(-119.51, 47.64) * mm, "mid": v(-119.7, 47.28) * mm, "end": v(-119.86, 46.9) * mm});
            skLineSegment(sketch, "E304", {"start": v(-119.51, 47.64) * mm, "end": v(-118.16, 49.51) * mm});
            skLineSegment(sketch, "E305", {"start": v(-118.16, 49.51) * mm, "end": v(-117.98, 49.86) * mm});
            skLineSegment(sketch, "E306", {"start": v(-117.98, 49.86) * mm, "end": v(-117.98, 49.93) * mm});
            skLineSegment(sketch, "E307", {"start": v(-117.98, 49.93) * mm, "end": v(-118.07, 50.11) * mm});
            skLineSegment(sketch, "E308", {"start": v(-118.07, 50.11) * mm, "end": v(-118.14, 50.14) * mm});
            skLineSegment(sketch, "E309", {"start": v(-118.14, 50.14) * mm, "end": v(-118.25, 50.12) * mm});
            skLineSegment(sketch, "E310", {"start": v(-118.25, 50.12) * mm, "end": v(-118.3, 50.08) * mm});
            skLineSegment(sketch, "E311", {"start": v(-118.3, 50.08) * mm, "end": v(-118.37, 50.02) * mm});
            skLineSegment(sketch, "E312", {"start": v(-118.37, 50.02) * mm, "end": v(-121.4, 47.01) * mm});
            skLineSegment(sketch, "E313", {"start": v(-121.4, 47.01) * mm, "end": v(-121.66, 46.8) * mm});
            skLineSegment(sketch, "E314", {"start": v(-121.66, 46.8) * mm, "end": v(-121.95, 46.76) * mm});
            skFitSpline(sketch, "E315", {"points": [v(-121.95, 46.76) * mm, v(-123.03, 46.76) * mm, v(-124.43, 47.16) * mm, v(-125.54, 47.85) * mm, v(-125.8, 48.18) * mm, v(-125.82, 48.45) * mm, v(-125.73, 48.73) * mm, v(-125.41, 49.1) * mm, v(-125.4, 49.1) * mm, v(-125.45, 49.06) * mm], "startDerivative": vector(-6.21, -0.37) * mm, "endDerivative": vector(-1.61, -1.5) * mm});
            skLineSegment(sketch, "E316", {"start": v(-125.4, 49.1) * mm, "end": v(-123.48, 50.96) * mm});
            skFitSpline(sketch, "E317", {"points": [v(-123.48, 50.96) * mm, v(-123.4, 51.1) * mm, v(-123.45, 51.22) * mm, v(-123.58, 51.33) * mm, v(-123.77, 51.26) * mm, v(-123.77, 51.26) * mm], "startDerivative": vector(0.45, 0.58) * mm, "endDerivative": vector(0.17, 0.07) * mm});
            skLineSegment(sketch, "E318", {"start": v(-123.77, 51.26) * mm, "end": v(-127.1, 49.63) * mm});
            skLineSegment(sketch, "E319", {"start": v(-127.1, 49.63) * mm, "end": v(-127.6, 49.46) * mm});
            skFitSpline(sketch, "E320", {"points": [v(-127.6, 49.46) * mm, v(-128.52, 49.46) * mm, v(-129.43, 50.17) * mm, v(-130.46, 50.9) * mm, v(-130.63, 51.26) * mm, v(-130.45, 51.55) * mm, v(-128.87, 52.38) * mm], "startDerivative": vector(-5.74, -0.95) * mm, "endDerivative": vector(8.34, 3.87) * mm});
            skFitSpline(sketch, "E321", {"points": [v(-128.87, 52.38) * mm, v(-127.18, 53.32) * mm, v(-126.26, 53.95) * mm, v(-126.18, 54.07) * mm, v(-126.34, 54.3) * mm, v(-126.56, 54.23) * mm, v(-127.4, 54.04) * mm, v(-129.2, 53.58) * mm, v(-129.9, 53.38) * mm, v(-131.02, 53.01) * mm, v(-131.47, 52.9) * mm, v(-132.27, 52.93) * mm, v(-132.75, 53.15) * mm, v(-133.16, 53.64) * mm, v(-134.33, 55.45) * mm, v(-134.33, 55.44) * mm], "startDerivative": vector(16.02, 8.44) * mm, "endDerivative": vector(0.53, -2.52) * mm});
            skFitSpline(sketch, "E322", {"points": [v(-134.33, 55.45) * mm, v(-134.4, 55.7) * mm, v(-134.33, 56) * mm, v(-134.15, 56.2) * mm, v(-133.46, 56.4) * mm, v(-132.22, 56.63) * mm, v(-130.65, 56.99) * mm, v(-129.44, 57.37) * mm, v(-129.17, 57.52) * mm, v(-129.16, 57.6) * mm, v(-129.93, 57.8) * mm, v(-132.09, 58.08) * mm, v(-134.67, 58.34) * mm, v(-135.31, 58.31) * mm, v(-135.3, 58.3) * mm], "startDerivative": vector(-2.57, 5.47) * mm, "endDerivative": vector(1.33, -0.59) * mm});
            skFitSpline(sketch, "E323", {"points": [v(-135.3, 58.3) * mm, v(-136.35, 59.52) * mm, v(-137.27, 61.16) * mm, v(-137.7, 62.15) * mm, v(-137.68, 62.52) * mm, v(-137.6, 62.66) * mm, v(-137.37, 62.75) * mm, v(-136.39, 62.72) * mm, v(-135.38, 62.6) * mm], "startDerivative": vector(-6.13, 6.37) * mm, "endDerivative": vector(6.9, -0.88) * mm});
            skFitSpline(sketch, "E324", {"points": [v(-135.38, 62.6) * mm, v(-133.34, 62.36) * mm, v(-131.3, 62.2) * mm, v(-130.74, 62.2) * mm, v(-130.74, 62.2) * mm], "startDerivative": vector(5.12, -0.68) * mm, "endDerivative": vector(0.22, 0) * mm});
            skFitSpline(sketch, "E325", {"points": [v(-130.74, 62.2) * mm, v(-130.65, 62.3) * mm, v(-130.7, 62.47) * mm, v(-130.79, 62.58) * mm], "startDerivative": vector(0.38, 0.24) * mm, "endDerivative": vector(-0.3, 0.27) * mm});
            skFitSpline(sketch, "E326", {"points": [v(-112.9, 57.85) * mm, v(-115.25, 59.48) * mm, v(-118.83, 60.79) * mm, v(-119.68, 61.04) * mm, v(-120.9, 62.2) * mm, v(-122, 64.06) * mm], "startDerivative": vector(-8.78, 7.3) * mm, "endDerivative": vector(-5.03, 9.6) * mm});
            skFitSpline(sketch, "E327", {"points": [v(-122, 64.06) * mm, v(-122.64, 65.82) * mm, v(-123.73, 68.49) * mm], "startDerivative": vector(-1.3, 3.75) * mm, "endDerivative": vector(-2.12, 5.06) * mm});
            skFitSpline(sketch, "E328", {"points": [v(-123.73, 68.49) * mm, v(-125.08, 71.6) * mm, v(-126.5, 74.68) * mm, v(-127.48, 76.2) * mm, v(-129.3, 78.86) * mm, v(-130.13, 79.87) * mm, v(-130.35, 80.16) * mm, v(-131.56, 80.97) * mm, v(-133.63, 82.07) * mm], "startDerivative": vector(-8.07, 18.5) * mm, "endDerivative": vector(-15.7, 7.97) * mm});
            skFitSpline(sketch, "E329", {"points": [v(-133.63, 82.07) * mm, v(-134.9, 82.64) * mm, v(-136.35, 83.24) * mm], "startDerivative": vector(-2.57, 1.17) * mm, "endDerivative": vector(-2.87, 1.16) * mm});
            skFitSpline(sketch, "E330", {"points": [v(-136.35, 83.24) * mm, v(-136.83, 83.24) * mm, v(-136.9, 82.86) * mm], "startDerivative": vector(-1.12, 0.21) * mm, "endDerivative": vector(0.06, -0.99) * mm});
            skFitSpline(sketch, "E331", {"points": [v(-136.9, 82.86) * mm, v(-136.83, 82.7) * mm, v(-136.69, 82.69) * mm, v(-135.85, 82.34) * mm, v(-134.48, 81.73) * mm, v(-133.73, 81.24) * mm, v(-132.53, 80.55) * mm, v(-131.62, 79.92) * mm, v(-131.44, 79.79) * mm, v(-131.07, 79.32) * mm, v(-130.68, 78.82) * mm, v(-130.45, 78.43) * mm, v(-130.36, 78.3) * mm, v(-130.35, 78.25) * mm], "startDerivative": vector(0.97, -4.84) * mm, "endDerivative": vector(0, -1.74) * mm});
            skFitSpline(sketch, "E332", {"points": [v(-130.35, 78.25) * mm, v(-130.4, 78.2) * mm, v(-130.76, 78.22) * mm], "startDerivative": vector(-0.09, -0.17) * mm, "endDerivative": vector(-0.64, 0.07) * mm});
            skFitSpline(sketch, "E333", {"points": [v(-130.76, 78.22) * mm, v(-131.67, 78.71) * mm, v(-133.18, 79.43) * mm, v(-138.8, 82.36) * mm, v(-143.44, 84.79) * mm, v(-147.13, 86.67) * mm, v(-149.08, 87.59) * mm, v(-150.17, 88.12) * mm, v(-150.49, 88.16) * mm], "startDerivative": vector(-10.83, 6.15) * mm, "endDerivative": vector(-6.15, -0.27) * mm});
            skFitSpline(sketch, "E334", {"points": [v(-150.49, 88.16) * mm, v(-150.49, 87.87) * mm, v(-150.28, 86.7) * mm, v(-149.5, 84.42) * mm, v(-148.77, 82.8) * mm, v(-148.02, 81.74) * mm, v(-147.02, 80.68) * mm, v(-146.25, 80.08) * mm, v(-145.34, 79.45) * mm, v(-143.76, 78.58) * mm, v(-140.6, 76.97) * mm], "startDerivative": vector(-0.28, -5.55) * mm, "endDerivative": vector(21.9, -11.08) * mm});
            skFitSpline(sketch, "E335", {"points": [v(-140.6, 76.97) * mm, v(-136.67, 74.99) * mm, v(-134.78, 73.95) * mm], "startDerivative": vector(7.3, -3.63) * mm, "endDerivative": vector(4.17, -2.34) * mm});
            skFitSpline(sketch, "E336", {"points": [v(-134.78, 73.95) * mm, v(-134.7, 73.82) * mm, v(-134.9, 73.57) * mm, v(-134.89, 73.58) * mm], "startDerivative": vector(0.38, -0.26) * mm, "endDerivative": vector(0.13, 0.07) * mm});
            skFitSpline(sketch, "E337", {"points": [v(-134.9, 73.57) * mm, v(-135.17, 73.64) * mm, v(-136.3, 74.14) * mm, v(-137.89, 74.86) * mm, v(-140.68, 76.06) * mm, v(-144.4, 77.6) * mm, v(-145.65, 78.05) * mm, v(-145.94, 78.02) * mm], "startDerivative": vector(-3.63, 0.65) * mm, "endDerivative": vector(-3.95, -0.88) * mm});
            skFitSpline(sketch, "E338", {"points": [v(-145.94, 78.02) * mm, v(-145.94, 77.52) * mm, v(-145.55, 76.42) * mm, v(-145.04, 75.06) * mm, v(-144.33, 73.92) * mm, v(-143.59, 73.12) * mm, v(-142.52, 72.34) * mm, v(-141.04, 71.53) * mm, v(-139.54, 70.93) * mm, v(-138.36, 70.48) * mm, v(-136.92, 69.85) * mm, v(-135.3, 69.1) * mm, v(-134.98, 68.95) * mm], "startDerivative": vector(-1.03, -8.6) * mm, "endDerivative": vector(5.51, -2.57) * mm});
            skFitSpline(sketch, "E339", {"points": [v(-134.98, 68.95) * mm, v(-134.34, 68.69) * mm, v(-134.31, 68.61) * mm, v(-134.37, 68.4) * mm, v(-134.49, 68.34) * mm], "startDerivative": vector(1.96, -0.7) * mm, "endDerivative": vector(-0.69, -0.2) * mm});
            skFitSpline(sketch, "E340", {"points": [v(-134.49, 68.34) * mm, v(-134.62, 68.34) * mm, v(-135.38, 68.6) * mm, v(-136.25, 68.93) * mm, v(-138.1, 69.57) * mm, v(-141.2, 70.61) * mm, v(-142.2, 70.96) * mm], "startDerivative": vector(-1.89, -0.3) * mm, "endDerivative": vector(-5.19, 1.83) * mm});
            skFitSpline(sketch, "E341", {"points": [v(-142.2, 70.96) * mm, v(-142.55, 70.96) * mm, v(-142.7, 70.8) * mm], "startDerivative": vector(-0.7, 0.1) * mm, "endDerivative": vector(-0.26, -0.44) * mm});
            skFitSpline(sketch, "E342", {"points": [v(-142.7, 70.8) * mm, v(-142.7, 70.42) * mm, v(-142.55, 70.09) * mm, v(-142.2, 69.36) * mm, v(-141.72, 68.62) * mm, v(-141.17, 67.77) * mm, v(-140.5, 66.85) * mm, v(-140.08, 66.33) * mm, v(-139.38, 65.4) * mm, v(-138.84, 64.84) * mm], "startDerivative": vector(-0.46, -5.15) * mm, "endDerivative": vector(4.64, -4.46) * mm});
            skFitSpline(sketch, "E343", {"points": [v(-138.84, 64.84) * mm, v(-138.27, 64.27) * mm, v(-137.82, 63.89) * mm, v(-137.06, 63.68) * mm, v(-135.89, 63.48) * mm, v(-134.9, 63.27) * mm, v(-133.83, 63.08) * mm, v(-132.59, 62.84) * mm, v(-131.62, 62.7) * mm, v(-131.04, 62.6) * mm, v(-130.79, 62.58) * mm], "startDerivative": vector(6, -6) * mm, "endDerivative": vector(4.12, -0.27) * mm});
            skFitSpline(sketch, "E344", {"points": [v(-105.24, 33.92) * mm, v(-104.45, 34.7) * mm, v(-104, 35.16) * mm, v(-103.35, 35.82) * mm, v(-102.84, 36.46) * mm], "startDerivative": vector(3.12, 2.88) * mm, "endDerivative": vector(1.63, 2.81) * mm});
            skFitSpline(sketch, "E345", {"points": [v(-102.84, 36.46) * mm, v(-102.68, 36.56) * mm, v(-102.55, 36.52) * mm], "startDerivative": vector(0.28, 0.25) * mm, "endDerivative": vector(0.29, -0.14) * mm});
            skFitSpline(sketch, "E346", {"points": [v(-102.55, 36.52) * mm, v(-102.41, 36.37) * mm, v(-101.96, 35.55) * mm, v(-101.63, 35) * mm, v(-101.28, 34.5) * mm, v(-100.73, 33.98) * mm, v(-100.03, 33.63) * mm, v(-99.27, 33.3) * mm, v(-97.94, 33.01) * mm], "startDerivative": vector(1.86, -1.64) * mm, "endDerivative": vector(8.38, -1.54) * mm});
            skFitSpline(sketch, "E347", {"points": [v(-97.94, 33.01) * mm, v(-97.19, 32.95) * mm, v(-96.04, 33.01) * mm, v(-95.4, 33.07) * mm, v(-94.13, 33.4) * mm, v(-93.22, 33.73) * mm, v(-91.56, 34.23) * mm, v(-90.22, 34.63) * mm, v(-89.2, 34.95) * mm, v(-87.04, 35.05) * mm, v(-85.77, 34.86) * mm], "startDerivative": vector(8.7, -1.2) * mm, "endDerivative": vector(10.97, -2.38) * mm});
            skFitSpline(sketch, "E348", {"points": [v(-85.77, 34.86) * mm, v(-84.26, 34.46) * mm, v(-83, 33.92) * mm, v(-82.17, 33.48) * mm], "startDerivative": vector(4.15, -0.94) * mm, "endDerivative": vector(2.73, -1.53) * mm});
            skFitSpline(sketch, "E349", {"points": [v(-82.17, 33.48) * mm, v(-81.03, 32.7) * mm, v(-80.04, 31.86) * mm, v(-80.05, 31.86) * mm], "startDerivative": vector(2.11, -1.29) * mm, "endDerivative": vector(-0.35, 0.06) * mm});
            skFitSpline(sketch, "E350", {"points": [v(-80.04, 31.86) * mm, v(-79.06, 30.81) * mm, v(-78.15, 29.5) * mm, v(-77.58, 28.6) * mm, v(-77, 27.46) * mm], "startDerivative": vector(3.85, -3.77) * mm, "endDerivative": vector(2.36, -4.87) * mm});
            skFitSpline(sketch, "E351", {"points": [v(-77, 27.46) * mm, v(-76.38, 26.26) * mm, v(-76.01, 25.42) * mm, v(-75.63, 24.32) * mm, v(-75.4, 23.36) * mm, v(-75.27, 22.5) * mm, v(-75.17, 21.9) * mm, v(-75.17, 20.94) * mm, v(-75.2, 20.13) * mm, v(-75.32, 19.63) * mm, v(-75.4, 19.3) * mm, v(-75.39, 19.29) * mm], "startDerivative": vector(5.25, -10.05) * mm, "endDerivative": vector(0.37, -0.81) * mm});
            skFitSpline(sketch, "E352", {"points": [v(-75.39, 19.29) * mm, v(-75.53, 19.4) * mm, v(-75.59, 19.66) * mm, v(-75.8, 20.42) * mm, v(-76.05, 21.2) * mm, v(-76.39, 21.97) * mm, v(-77.36, 23.37) * mm, v(-79.44, 24.95) * mm, v(-81.83, 25.62) * mm, v(-85.66, 25.68) * mm, v(-89, 25.15) * mm, v(-89.72, 24.88) * mm], "startDerivative": vector(-4.8, 3.1) * mm, "endDerivative": vector(-7.42, -3.8) * mm});
            skFitSpline(sketch, "E353", {"points": [v(-108.34, 35.54) * mm, v(-108.4, 35.47) * mm, v(-108.34, 34.9) * mm, v(-107.9, 33.9) * mm, v(-107.26, 32.7) * mm], "startDerivative": vector(-0.73, -0.5) * mm, "endDerivative": vector(1.82, -3.43) * mm});
            skLineSegment(sketch, "E354", {"start": v(-104.37, 28.05) * mm, "end": v(-104.37, 28.05) * mm});
            skLineSegment(sketch, "E355", {"start": v(-113.33, 62.9) * mm, "end": v(-106.9, 59.46) * mm});
            skLineSegment(sketch, "E356", {"start": v(-106.9, 59.46) * mm, "end": v(-106.83, 59.43) * mm});
            skLineSegment(sketch, "E357", {"start": v(-106.83, 59.43) * mm, "end": v(-106.8, 59.43) * mm});
            skLineSegment(sketch, "E358", {"start": v(-106.8, 59.43) * mm, "end": v(-106.78, 59.46) * mm});
            skLineSegment(sketch, "E359", {"start": v(-106.78, 59.46) * mm, "end": v(-106.8, 59.54) * mm});
            skLineSegment(sketch, "E360", {"start": v(-106.8, 59.54) * mm, "end": v(-106.86, 59.65) * mm});
            skLineSegment(sketch, "E361", {"start": v(-113.33, 62.9) * mm, "end": v(-115.02, 67.75) * mm});
            skLineSegment(sketch, "E362", {"start": v(-115.02, 67.75) * mm, "end": v(-115.02, 67.82) * mm});
            skLineSegment(sketch, "E363", {"start": v(-115.02, 67.82) * mm, "end": v(-114.96, 67.82) * mm});
            skLineSegment(sketch, "E364", {"start": v(-114.96, 67.82) * mm, "end": v(-109.92, 66) * mm});
            skLineSegment(sketch, "E365", {"start": v(-109.92, 66) * mm, "end": v(-109.85, 65.95) * mm});
            skLineSegment(sketch, "E366", {"start": v(-109.85, 65.95) * mm, "end": v(-109.8, 65.83) * mm});
            skLineSegment(sketch, "E367", {"start": v(-109.8, 65.83) * mm, "end": v(-106.86, 59.65) * mm});
            skLineSegment(sketch, "E368", {"start": v(-102.74, 66.16) * mm, "end": v(-105.9, 59.76) * mm});
            skLineSegment(sketch, "E369", {"start": v(-105.9, 59.76) * mm, "end": v(-105.96, 59.72) * mm});
            skLineSegment(sketch, "E370", {"start": v(-105.96, 59.72) * mm, "end": v(-106.06, 59.77) * mm});
            skLineSegment(sketch, "E371", {"start": v(-106.06, 59.77) * mm, "end": v(-109.1, 66.18) * mm});
            skLineSegment(sketch, "E372", {"start": v(-109.1, 66.18) * mm, "end": v(-109.15, 66.3) * mm});
            skLineSegment(sketch, "E373", {"start": v(-109.15, 66.3) * mm, "end": v(-109.15, 66.39) * mm});
            skLineSegment(sketch, "E374", {"start": v(-109.15, 66.39) * mm, "end": v(-106, 73.58) * mm});
            skLineSegment(sketch, "E375", {"start": v(-106, 73.58) * mm, "end": v(-105.95, 73.64) * mm});
            skLineSegment(sketch, "E376", {"start": v(-105.95, 73.64) * mm, "end": v(-105.9, 73.58) * mm});
            skLineSegment(sketch, "E377", {"start": v(-105.9, 73.58) * mm, "end": v(-102.74, 66.4) * mm});
            skLineSegment(sketch, "E378", {"start": v(-102.74, 66.4) * mm, "end": v(-102.7, 66.3) * mm});
            skLineSegment(sketch, "E379", {"start": v(-102.7, 66.3) * mm, "end": v(-102.69, 66.26) * mm});
            skLineSegment(sketch, "E380", {"start": v(-102.69, 66.26) * mm, "end": v(-102.74, 66.16) * mm});
            skLineSegment(sketch, "E381", {"start": v(-105.16, 59.38) * mm, "end": v(-99.04, 62.32) * mm});
            skPoint(sketch, "E381.startSnap0", {"position": v(-103.74, 59.38) * mm});
            skLineSegment(sketch, "E382", {"start": v(-99.04, 62.32) * mm, "end": v(-98.84, 62.48) * mm});
            skLineSegment(sketch, "E383", {"start": v(-98.84, 62.48) * mm, "end": v(-98.65, 63.01) * mm});
            skLineSegment(sketch, "E384", {"start": v(-98.65, 63.01) * mm, "end": v(-96.88, 67.71) * mm});
            skLineSegment(sketch, "E385", {"start": v(-96.88, 67.71) * mm, "end": v(-96.88, 67.82) * mm});
            skLineSegment(sketch, "E386", {"start": v(-96.88, 67.82) * mm, "end": v(-96.99, 67.84) * mm});
            skLineSegment(sketch, "E387", {"start": v(-96.99, 67.84) * mm, "end": v(-101.84, 66.16) * mm});
            skLineSegment(sketch, "E388", {"start": v(-101.84, 66.16) * mm, "end": v(-101.92, 66.13) * mm});
            skLineSegment(sketch, "E389", {"start": v(-101.92, 66.13) * mm, "end": v(-101.99, 66.03) * mm});
            skLineSegment(sketch, "E390", {"start": v(-101.99, 66.03) * mm, "end": v(-105.19, 59.54) * mm});
            skLineSegment(sketch, "E391", {"start": v(-105.19, 59.54) * mm, "end": v(-105.23, 59.44) * mm});
            skLineSegment(sketch, "E392", {"start": v(-105.23, 59.44) * mm, "end": v(-105.23, 59.38) * mm});
            skLineSegment(sketch, "E393", {"start": v(-105.23, 59.38) * mm, "end": v(-105.16, 59.38) * mm});
            skFitSpline(sketch, "E394", {"points": [v(-133.84, 1.94) * mm, v(-133.27, 1.34) * mm, v(-131.73, 0.59) * mm, v(-129.91, 1.03) * mm, v(-128.75, 1.71) * mm, v(-127.72, 3.15) * mm, v(-127.15, 4.48) * mm], "startDerivative": vector(3.78, -4.6) * mm, "endDerivative": vector(2.92, 7.9) * mm});
            skFitSpline(sketch, "E395", {"points": [v(-127.15, 4.48) * mm, v(-126.8, 4.04) * mm, v(-126, 3) * mm, v(-125.69, 2.76) * mm, v(-125.64, 2.74) * mm], "startDerivative": vector(1.15, -1.32) * mm, "endDerivative": vector(0.44, -0.11) * mm});
            skFitSpline(sketch, "E396", {"points": [v(-125.64, 2.74) * mm, v(-125.59, 2.74) * mm], "startDerivative": vector(0.06, 0) * mm, "endDerivative": vector(0.06, 0) * mm});
            skFitSpline(sketch, "E397", {"points": [v(-125.59, 2.74) * mm, v(-125.7, 3.15) * mm, v(-125.96, 4.13) * mm, v(-126.25, 6.83) * mm, v(-125.86, 9.39) * mm, v(-124.62, 11.57) * mm, v(-122.96, 12.7) * mm, v(-121.39, 13.12) * mm, v(-118.25, 13.1) * mm, v(-115.77, 12.56) * mm], "startDerivative": vector(-2, 7.25) * mm, "endDerivative": vector(18.32, -5.01) * mm});
            skFitSpline(sketch, "E398", {"points": [v(-115.77, 12.56) * mm, v(-113, 11.33) * mm, v(-109.81, 9.36) * mm, v(-107.43, 7.86) * mm, v(-104.98, 6.3) * mm, v(-101.7, 4.3) * mm, v(-99.72, 3.02) * mm, v(-96.81, 1.88) * mm, v(-93.32, 1.2) * mm, v(-90.28, 1.5) * mm, v(-88.9, 1.8) * mm, v(-86.3, 2.94) * mm, v(-83.07, 5.18) * mm], "startDerivative": vector(32.57, -12.8) * mm, "endDerivative": vector(33.57, 25.37) * mm});
            skFitSpline(sketch, "E399", {"points": [v(-83.07, 5.18) * mm, v(-81.88, 6.28) * mm, v(-80.33, 8) * mm, v(-78.87, 10.15) * mm, v(-77.6, 12.45) * mm, v(-76.98, 13.98) * mm, v(-76.64, 15.03) * mm, v(-76.5, 16.75) * mm, v(-76.5, 18.23) * mm], "startDerivative": vector(9.94, 8.8) * mm, "endDerivative": vector(-0.06, 12.7) * mm});
            skFitSpline(sketch, "E400", {"points": [v(-76.5, 18.23) * mm, v(-76.84, 20.16) * mm, v(-77.86, 22.14) * mm, v(-78.97, 23.35) * mm, v(-80.46, 24.15) * mm, v(-81.98, 24.5) * mm, v(-83.3, 24.5) * mm, v(-84.12, 24.08) * mm], "startDerivative": vector(-1.3, 12.08) * mm, "endDerivative": vector(-6.88, -4.77) * mm});
            skFitSpline(sketch, "E401", {"points": [v(-133.84, 1.94) * mm, v(-132.22, 2.32) * mm, v(-130.56, 3.4) * mm, v(-129.78, 5.32) * mm, v(-129.68, 7.12) * mm], "startDerivative": vector(6.83, 1.12) * mm, "endDerivative": vector(-0.02, 7.22) * mm});
            skFitSpline(sketch, "E402", {"points": [v(-129.68, 7.12) * mm, v(-129.52, 9.9) * mm, v(-128.61, 12.9) * mm, v(-126.94, 15.23) * mm, v(-125.43, 16.37) * mm, v(-123.45, 17.3) * mm, v(-121.3, 17.8) * mm, v(-118.48, 17.94) * mm, v(-115.66, 17.51) * mm, v(-112.7, 16.48) * mm], "startDerivative": vector(0.36, 24.1) * mm, "endDerivative": vector(24.45, -9.48) * mm});
            skFitSpline(sketch, "E403", {"points": [v(-84.12, 24.08) * mm, v(-84.36, 23.73) * mm, v(-84.6, 23.16) * mm, v(-85.27, 22.04) * mm, v(-86.37, 20.49) * mm], "startDerivative": vector(-1.54, -2) * mm, "endDerivative": vector(-3.26, -4.57) * mm});
            skFitSpline(sketch, "E404", {"points": [v(-112.7, 16.48) * mm, v(-111.1, 15.72) * mm, v(-108.05, 14.26) * mm, v(-104.93, 12.83) * mm], "startDerivative": vector(5.55, -2.63) * mm, "endDerivative": vector(8.32, -3.78) * mm});
            skFitSpline(sketch, "E405", {"points": [v(-97.67, 12.08) * mm, v(-96.08, 12.56) * mm, v(-93.62, 13.9) * mm, v(-90.8, 15.93) * mm, v(-88.35, 18.04) * mm, v(-86.37, 20.49) * mm], "startDerivative": vector(8.03, 1.42) * mm, "endDerivative": vector(8.67, 11.75) * mm});
            skFitSpline(sketch, "E406", {"points": [v(-97.67, 12.08) * mm, v(-99.78, 11.7) * mm, v(-102.82, 11.95) * mm, v(-104.93, 12.83) * mm], "startDerivative": vector(-6.36, -1.52) * mm, "endDerivative": vector(-6.1, 3.12) * mm});
            skFitSpline(sketch, "E407", {"points": [v(-81.7, 78.96) * mm, v(-81.54, 79.35) * mm, v(-80.91, 80.22) * mm, v(-80.21, 80.86) * mm, v(-78.46, 81.93) * mm, v(-77.46, 82.45) * mm, v(-75.88, 83.22) * mm, v(-75.55, 83.34) * mm, v(-75.12, 83.54) * mm, v(-75.15, 83.9) * mm, v(-75.3, 84.03) * mm, v(-75.75, 83.96) * mm, v(-78.17, 82.9) * mm, v(-80.17, 81.83) * mm, v(-81.33, 81.06) * mm, v(-82.39, 80.01) * mm, v(-83.57, 78.32) * mm], "startDerivative": vector(3.02, 8.72) * mm, "endDerivative": vector(-13.4, -20.7) * mm});
            skFitSpline(sketch, "E408", {"points": [v(-83.57, 78.32) * mm, v(-84.92, 76.38) * mm, v(-85.97, 74.4) * mm, v(-86.56, 73.09) * mm, v(-87.3, 71.36) * mm], "startDerivative": vector(-5.1, -6.84) * mm, "endDerivative": vector(-3.17, -7.4) * mm});
            skFitSpline(sketch, "E409", {"points": [v(-87.3, 71.36) * mm, v(-87.9, 70.03) * mm, v(-89.04, 67.21) * mm, v(-90.14, 64.48) * mm, v(-91.04, 62.91) * mm, v(-91.91, 62.1) * mm, v(-92.84, 61.6) * mm, v(-94.08, 61.29) * mm], "startDerivative": vector(-4.3, -9.17) * mm, "endDerivative": vector(-10.63, -2.23) * mm});
            skFitSpline(sketch, "E410", {"points": [v(-81.7, 78.96) * mm, v(-81.33, 78.96) * mm, v(-80.05, 79.54) * mm, v(-78.02, 80.58) * mm, v(-74.47, 82.4) * mm, v(-70.73, 84.37) * mm, v(-66.52, 86.58) * mm, v(-64.46, 87.63) * mm, v(-62.2, 88.7) * mm, v(-61.6, 88.9) * mm], "startDerivative": vector(7.2, -1.13) * mm, "endDerivative": vector(8.31, 2.16) * mm});
            skFitSpline(sketch, "E411", {"points": [v(-61.6, 88.9) * mm, v(-61.53, 88.92) * mm], "startDerivative": vector(0.07, 0.02) * mm, "endDerivative": vector(0.07, 0.02) * mm});
            skFitSpline(sketch, "E412", {"points": [v(-61.53, 88.92) * mm, v(-61.5, 88.86) * mm, v(-61.5, 88.38) * mm, v(-61.55, 88.02) * mm, v(-61.72, 87.33) * mm, v(-62.1, 86.18) * mm], "startDerivative": vector(0.54, -0.48) * mm, "endDerivative": vector(-1.35, -3.78) * mm});
            skFitSpline(sketch, "E413", {"points": [v(-62.1, 86.18) * mm, v(-62.61, 84.82) * mm, v(-63.3, 83.48) * mm, v(-63.78, 82.77) * mm], "startDerivative": vector(-1.31, -3.73) * mm, "endDerivative": vector(-1.72, -2.3) * mm});
            skFitSpline(sketch, "E414", {"points": [v(-63.78, 82.77) * mm, v(-64.64, 81.82) * mm, v(-65.22, 81.24) * mm, v(-66.16, 80.5) * mm, v(-67.08, 79.94) * mm, v(-68.3, 79.3) * mm, v(-69.69, 78.58) * mm, v(-70.7, 78.06) * mm], "startDerivative": vector(-6.17, -6.93) * mm, "endDerivative": vector(-6.99, -3.49) * mm});
            skFitSpline(sketch, "E415", {"points": [v(-70.7, 78.06) * mm, v(-71.9, 77.46) * mm, v(-73.15, 76.8) * mm, v(-74.26, 76.23) * mm], "startDerivative": vector(-3.56, -1.78) * mm, "endDerivative": vector(-3.38, -1.75) * mm});
            skFitSpline(sketch, "E416", {"points": [v(-74.26, 76.23) * mm, v(-76.12, 75.25) * mm, v(-77.04, 74.83) * mm, v(-77.2, 74.73) * mm, v(-77.27, 74.51) * mm, v(-77.18, 74.34) * mm, v(-77, 74.3) * mm, v(-76.38, 74.55) * mm], "startDerivative": vector(-5.62, -2.93) * mm, "endDerivative": vector(4.52, 2.34) * mm});
            skFitSpline(sketch, "E417", {"points": [v(-66.12, 77.97) * mm, v(-66.54, 76.93) * mm, v(-67.1, 75.53) * mm, v(-67.79, 74.58) * mm, v(-68.15, 74.15) * mm, v(-69, 73.4) * mm, v(-70.2, 72.65) * mm], "startDerivative": vector(-2.57, -5.96) * mm, "endDerivative": vector(-6.62, -3.73) * mm});
            skFitSpline(sketch, "E418", {"points": [v(-70.2, 72.65) * mm, v(-70.76, 72.35) * mm, v(-71.79, 71.92) * mm, v(-72.28, 71.75) * mm, v(-73.01, 71.5) * mm, v(-73.94, 71.1) * mm, v(-75.18, 70.54) * mm, v(-76.11, 70.12) * mm, v(-77.13, 69.68) * mm, v(-77.64, 69.46) * mm, v(-77.7, 69.33) * mm, v(-77.67, 69.19) * mm, v(-77.55, 69.07) * mm, v(-77.36, 69.14) * mm], "startDerivative": vector(-6.12, -3.6) * mm, "endDerivative": vector(4.38, 2.7) * mm});
            skFitSpline(sketch, "E419", {"points": [v(-66.12, 77.97) * mm, v(-66.07, 78.22) * mm, v(-66.08, 78.77) * mm, v(-66.48, 78.76) * mm, v(-67.27, 78.45) * mm, v(-68.8, 77.83) * mm, v(-69.67, 77.48) * mm, v(-70.7, 77.03) * mm, v(-71.65, 76.63) * mm], "startDerivative": vector(0.73, 2.83) * mm, "endDerivative": vector(-6.55, -2.7) * mm});
            skFitSpline(sketch, "E420", {"points": [v(-71.65, 76.63) * mm, v(-72.3, 76.35) * mm, v(-73.48, 75.82) * mm, v(-74.72, 75.3) * mm, v(-76.02, 74.71) * mm, v(-76.38, 74.55) * mm], "startDerivative": vector(-3.57, -1.47) * mm, "endDerivative": vector(-3.02, -1.54) * mm});
            skFitSpline(sketch, "E421", {"points": [v(-77.36, 69.14) * mm, v(-76.1, 69.54) * mm, v(-73.95, 70.3) * mm, v(-71.84, 71) * mm, v(-70.4, 71.52) * mm], "startDerivative": vector(5.5, 1.7) * mm, "endDerivative": vector(5.96, 2.18) * mm});
            skFitSpline(sketch, "E422", {"points": [v(-70.4, 71.52) * mm, v(-69.71, 71.75) * mm], "startDerivative": vector(0.7, 0.23) * mm, "endDerivative": vector(0.7, 0.23) * mm});
            skFitSpline(sketch, "E423", {"points": [v(-69.71, 71.75) * mm, v(-69.54, 71.7) * mm, v(-69.36, 71.52) * mm, v(-69.43, 70.98) * mm, v(-69.8, 70.26) * mm, v(-70.3, 69.4) * mm], "startDerivative": vector(1.43, -0.19) * mm, "endDerivative": vector(-1.9, -3.2) * mm});
            skFitSpline(sketch, "E424", {"points": [v(-70.3, 69.4) * mm, v(-72.4, 66.47) * mm, v(-74.24, 64.7) * mm, v(-74.57, 64.57) * mm, v(-77.34, 63.96) * mm, v(-80.56, 63.42) * mm], "startDerivative": vector(-7.68, -11.87) * mm, "endDerivative": vector(-12.86, -1.93) * mm});
            skFitSpline(sketch, "E425", {"points": [v(-80.56, 63.42) * mm, v(-81.2, 63.34) * mm, v(-81.33, 63.26) * mm, v(-81.43, 63.14) * mm, v(-81.25, 62.91) * mm, v(-80.88, 62.92) * mm, v(-79.24, 63.03) * mm], "startDerivative": vector(-3.87, -0.23) * mm, "endDerivative": vector(6.1, 0.27) * mm});
            skFitSpline(sketch, "E426", {"points": [v(-79.24, 63.03) * mm, v(-76.55, 63.33) * mm, v(-74.67, 63.5) * mm, v(-74.32, 63.27) * mm, v(-74.44, 62.53) * mm, v(-75.38, 60.75) * mm], "startDerivative": vector(9.74, 0.96) * mm, "endDerivative": vector(-4.65, -7.99) * mm});
            skFitSpline(sketch, "E427", {"points": [v(-75.38, 60.75) * mm, v(-76.58, 59.14) * mm, v(-76.8, 59.1) * mm, v(-78.81, 58.94) * mm, v(-80.8, 58.76) * mm, v(-82.55, 58.49) * mm, v(-82.85, 58.29) * mm, v(-82.04, 57.93) * mm, v(-79.53, 57.33) * mm], "startDerivative": vector(-9.68, -14.1) * mm, "endDerivative": vector(15.37, -3.36) * mm});
            skFitSpline(sketch, "E428", {"points": [v(-79.53, 57.33) * mm, v(-77.81, 56.9) * mm, v(-77.65, 56.43) * mm, v(-78.7, 54.68) * mm, v(-79.1, 54.1) * mm, v(-79.7, 53.75) * mm, v(-80.6, 53.69) * mm, v(-81.61, 54.03) * mm, v(-83.8, 54.62) * mm, v(-85.48, 55.02) * mm, v(-85.62, 55.05) * mm], "startDerivative": vector(16.32, -2.74) * mm, "endDerivative": vector(-2.77, 0.57) * mm});
            skFitSpline(sketch, "E429", {"points": [v(-85.62, 55.05) * mm, v(-85.78, 55.05) * mm, v(-85.9, 54.78) * mm, v(-85.48, 54.43) * mm, v(-84.43, 53.81) * mm, v(-82.08, 52.57) * mm, v(-81.53, 52.23) * mm, v(-81.44, 51.93) * mm, v(-82.19, 51.27) * mm, v(-83.22, 50.48) * mm, v(-83.61, 50.2) * mm, v(-84.43, 50.24) * mm, v(-86.72, 51.18) * mm, v(-88.16, 51.96) * mm], "startDerivative": vector(-5.17, 1.41) * mm, "endDerivative": vector(-12.5, 7.09) * mm});
            skFitSpline(sketch, "E430", {"points": [v(-88.16, 51.96) * mm, v(-88.34, 52.05) * mm, v(-88.5, 52.03) * mm, v(-88.61, 51.87) * mm, v(-88.05, 51.22) * mm, v(-86.88, 50.15) * mm, v(-86.25, 49.29) * mm, v(-86.3, 48.88) * mm, v(-86.91, 48.34) * mm, v(-88.53, 47.62) * mm, v(-90.15, 47.55) * mm, v(-90.48, 47.61) * mm, v(-90.78, 47.87) * mm, v(-91.22, 48.28) * mm, v(-92.65, 49.76) * mm, v(-93.78, 50.9) * mm, v(-94.07, 50.72) * mm, v(-93.62, 49.98) * mm], "startDerivative": vector(-5.9, 3.93) * mm, "endDerivative": vector(11.47, -13.36) * mm});
            skFitSpline(sketch, "E431", {"points": [v(-93.62, 49.98) * mm, v(-93.16, 49.4) * mm, v(-92.23, 48.02) * mm, v(-92.12, 47.52) * mm, v(-92.1, 47.2) * mm, v(-92.39, 46.4) * mm, v(-93.42, 45.87) * mm, v(-94.52, 45.74) * mm, v(-95.32, 45.92) * mm, v(-96.18, 46.47) * mm, v(-96.83, 47.42) * mm, v(-98.14, 49.47) * mm, v(-99.81, 51.99) * mm, v(-100.86, 53.56) * mm, v(-101.03, 53.85) * mm, v(-101.1, 54.1) * mm, v(-101.17, 55.61) * mm, v(-100.5, 57.15) * mm, v(-99.15, 58.58) * mm, v(-97.87, 59.55) * mm, v(-95.9, 60.6) * mm, v(-94.92, 61) * mm, v(-94.08, 61.29) * mm], "startDerivative": vector(10.9, -13.21) * mm, "endDerivative": vector(21.4, 7.23) * mm});
            skFitSpline(sketch, "E432", {"points": [v(-77.24, 28.9) * mm, v(-77.22, 28.84) * mm, v(-77.2, 28.8) * mm], "startDerivative": vector(0.02, -0.1) * mm, "endDerivative": vector(0.04, -0.07) * mm});
            skFitSpline(sketch, "E433", {"points": [v(-104.31, 28.04) * mm, v(-101.52, 25.67) * mm, v(-97.97, 24.26) * mm, v(-94.55, 24.03) * mm, v(-91.87, 24.3) * mm, v(-90.55, 24.64) * mm, v(-89.72, 24.88) * mm], "startDerivative": vector(3.08, -2.9) * mm, "endDerivative": vector(7.6, 2.23) * mm});
            skFitSpline(sketch, "E434", {"points": [v(-105.24, 33.92) * mm, v(-105.53, 33.63) * mm, v(-105.76, 33.35) * mm, v(-105.87, 33.18) * mm, v(-105.9, 33.16) * mm, v(-105.93, 33.15) * mm, v(-106.01, 33.24) * mm, v(-106.01, 33.24) * mm], "startDerivative": vector(-1.16, -1.1) * mm, "endDerivative": vector(0.14, -0.01) * mm});
            skFitSpline(sketch, "E435", {"points": [v(-106.01, 33.24) * mm, v(-106.42, 33.64) * mm, v(-106.85, 34.05) * mm, v(-107.35, 34.56) * mm, v(-108.01, 35.25) * mm, v(-108.27, 35.51) * mm, v(-108.34, 35.54) * mm], "startDerivative": vector(-2.25, 2.23) * mm, "endDerivative": vector(-0.95, 0.25) * mm});
            skFitSpline(sketch, "E436", {"points": [v(-107.26, 32.7) * mm, v(-106.41, 31.15) * mm, v(-105.67, 29.88) * mm, v(-104.85, 28.63) * mm, v(-104.31, 28.04) * mm], "startDerivative": vector(3.02, -5.64) * mm, "endDerivative": vector(2.72, -2.67) * mm});
            skSolve(sketch);
        }
        {
            var Q0;
            Q0 = qSketchRegion(id + "F2", true);
            extrude(context, id + "F3", {"entities" : qUnion([Q0]), "depth" : 3.17 * mm});
        }
    });
